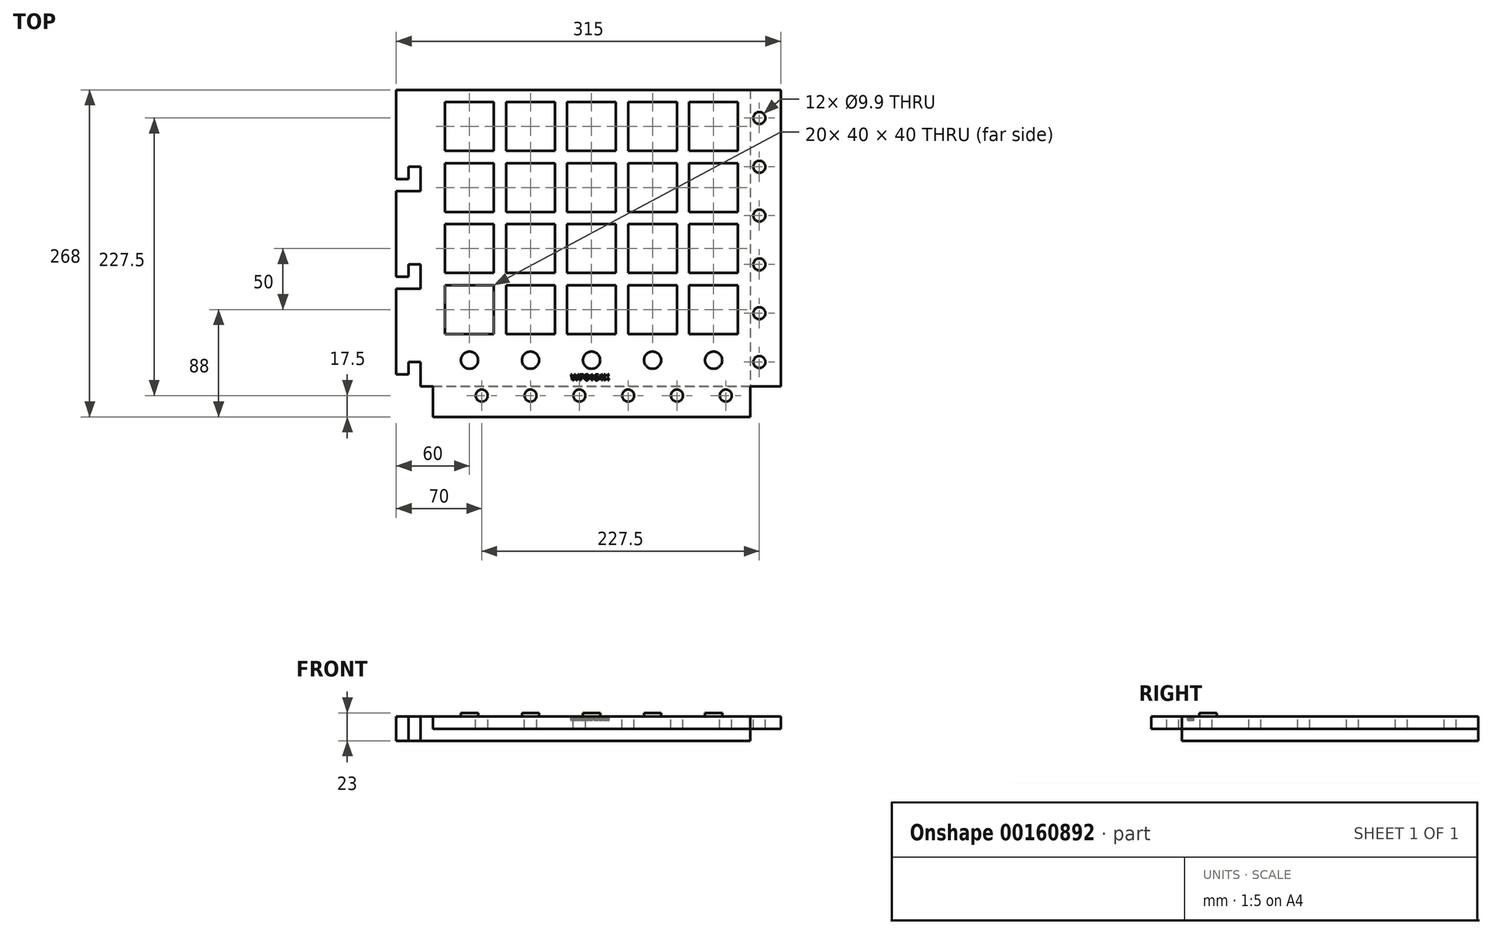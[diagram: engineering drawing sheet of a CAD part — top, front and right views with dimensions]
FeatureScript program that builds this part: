
annotation { "Feature Type Name" : "Feature", "Feature Type Description" : "" }
export const myFeature = defineFeature(function(context is Context, id is Id, definition is map)
    precondition{}
    {
        {
            var Q0;
            Q0=qCreatedBy(makeId("Top.planeOp"),FACE);
            var sketch = newSketch(context, id + "F0", { "sketchPlane" : qUnion([Q0])});
            skLineSegment(sketch, "E0", {"start": v(-205.43, 0) * mm, "end": v(243.02, 0) * mm, "construction": true});
            skLineSegment(sketch, "E1", {"start": v(0, 205.1) * mm, "end": v(0, -211.65) * mm, "construction": true});
            skLineSegment(sketch, "E2.bottom", {"start": v(130, 105) * mm, "end": v(-130, 105) * mm});
            skLineSegment(sketch, "E2.top", {"start": v(130, -105) * mm, "end": v(-130, -105) * mm});
            skLineSegment(sketch, "E2.left", {"start": v(130, 105) * mm, "end": v(130, -105) * mm});
            skLineSegment(sketch, "E2.right", {"start": v(-130, 105) * mm, "end": v(-130, -105) * mm});
            skPoint(sketch, "E2.middle", {"position": v(0, 0) * mm});
            skLineSegment(sketch, "E3.bottom", {"start": v(80, -55) * mm, "end": v(120, -55) * mm});
            skLineSegment(sketch, "E3.top", {"start": v(80, -95) * mm, "end": v(120, -95) * mm});
            skLineSegment(sketch, "E3.left", {"start": v(80, -55) * mm, "end": v(80, -95) * mm});
            skLineSegment(sketch, "E3.right", {"start": v(120, -55) * mm, "end": v(120, -95) * mm});
            skLineSegment(sketch, "E4.0.1.0", {"start": v(80, -5) * mm, "end": v(120, -5) * mm});
            skLineSegment(sketch, "E4.0.1.1", {"start": v(120, -5) * mm, "end": v(120, -45) * mm});
            skLineSegment(sketch, "E4.0.1.2", {"start": v(80, -45) * mm, "end": v(120, -45) * mm});
            skLineSegment(sketch, "E4.0.1.3", {"start": v(80, -5) * mm, "end": v(80, -45) * mm});
            skLineSegment(sketch, "E4.0.2.0", {"start": v(80, 45) * mm, "end": v(120, 45) * mm});
            skLineSegment(sketch, "E4.0.2.1", {"start": v(120, 45) * mm, "end": v(120, 5) * mm});
            skLineSegment(sketch, "E4.0.2.2", {"start": v(80, 5) * mm, "end": v(120, 5) * mm});
            skLineSegment(sketch, "E4.0.2.3", {"start": v(80, 45) * mm, "end": v(80, 5) * mm});
            skLineSegment(sketch, "E4.0.3.0", {"start": v(80, 95) * mm, "end": v(120, 95) * mm});
            skLineSegment(sketch, "E4.0.3.1", {"start": v(120, 95) * mm, "end": v(120, 55) * mm});
            skLineSegment(sketch, "E4.0.3.2", {"start": v(80, 55) * mm, "end": v(120, 55) * mm});
            skLineSegment(sketch, "E4.0.3.3", {"start": v(80, 95) * mm, "end": v(80, 55) * mm});
            skLineSegment(sketch, "E4.1.0.0", {"start": v(30, -55) * mm, "end": v(70, -55) * mm});
            skLineSegment(sketch, "E4.1.0.1", {"start": v(70, -55) * mm, "end": v(70, -95) * mm});
            skLineSegment(sketch, "E4.1.0.2", {"start": v(30, -95) * mm, "end": v(70, -95) * mm});
            skLineSegment(sketch, "E4.1.0.3", {"start": v(30, -55) * mm, "end": v(30, -95) * mm});
            skLineSegment(sketch, "E4.1.1.0", {"start": v(30, -5) * mm, "end": v(70, -5) * mm});
            skLineSegment(sketch, "E4.1.1.1", {"start": v(70, -5) * mm, "end": v(70, -45) * mm});
            skLineSegment(sketch, "E4.1.1.2", {"start": v(30, -45) * mm, "end": v(70, -45) * mm});
            skLineSegment(sketch, "E4.1.1.3", {"start": v(30, -5) * mm, "end": v(30, -45) * mm});
            skLineSegment(sketch, "E4.1.2.0", {"start": v(30, 45) * mm, "end": v(70, 45) * mm});
            skLineSegment(sketch, "E4.1.2.1", {"start": v(70, 45) * mm, "end": v(70, 5) * mm});
            skLineSegment(sketch, "E4.1.2.2", {"start": v(30, 5) * mm, "end": v(70, 5) * mm});
            skLineSegment(sketch, "E4.1.2.3", {"start": v(30, 45) * mm, "end": v(30, 5) * mm});
            skLineSegment(sketch, "E4.1.3.0", {"start": v(30, 95) * mm, "end": v(70, 95) * mm});
            skLineSegment(sketch, "E4.1.3.1", {"start": v(70, 95) * mm, "end": v(70, 55) * mm});
            skLineSegment(sketch, "E4.1.3.2", {"start": v(30, 55) * mm, "end": v(70, 55) * mm});
            skLineSegment(sketch, "E4.1.3.3", {"start": v(30, 95) * mm, "end": v(30, 55) * mm});
            skLineSegment(sketch, "E4.2.0.0", {"start": v(-20, -55) * mm, "end": v(20, -55) * mm});
            skLineSegment(sketch, "E4.2.0.1", {"start": v(20, -55) * mm, "end": v(20, -95) * mm});
            skLineSegment(sketch, "E4.2.0.2", {"start": v(-20, -95) * mm, "end": v(20, -95) * mm});
            skLineSegment(sketch, "E4.2.0.3", {"start": v(-20, -55) * mm, "end": v(-20, -95) * mm});
            skLineSegment(sketch, "E4.2.1.0", {"start": v(-20, -5) * mm, "end": v(20, -5) * mm});
            skLineSegment(sketch, "E4.2.1.1", {"start": v(20, -5) * mm, "end": v(20, -45) * mm});
            skLineSegment(sketch, "E4.2.1.2", {"start": v(-20, -45) * mm, "end": v(20, -45) * mm});
            skLineSegment(sketch, "E4.2.1.3", {"start": v(-20, -5) * mm, "end": v(-20, -45) * mm});
            skLineSegment(sketch, "E4.2.2.0", {"start": v(-20, 45) * mm, "end": v(20, 45) * mm});
            skLineSegment(sketch, "E4.2.2.1", {"start": v(20, 45) * mm, "end": v(20, 5) * mm});
            skLineSegment(sketch, "E4.2.2.2", {"start": v(-20, 5) * mm, "end": v(20, 5) * mm});
            skLineSegment(sketch, "E4.2.2.3", {"start": v(-20, 45) * mm, "end": v(-20, 5) * mm});
            skLineSegment(sketch, "E4.2.3.0", {"start": v(-20, 95) * mm, "end": v(20, 95) * mm});
            skLineSegment(sketch, "E4.2.3.1", {"start": v(20, 95) * mm, "end": v(20, 55) * mm});
            skLineSegment(sketch, "E4.2.3.2", {"start": v(-20, 55) * mm, "end": v(20, 55) * mm});
            skLineSegment(sketch, "E4.2.3.3", {"start": v(-20, 95) * mm, "end": v(-20, 55) * mm});
            skLineSegment(sketch, "E4.3.0.0", {"start": v(-70, -55) * mm, "end": v(-30, -55) * mm});
            skLineSegment(sketch, "E4.3.0.1", {"start": v(-30, -55) * mm, "end": v(-30, -95) * mm});
            skLineSegment(sketch, "E4.3.0.2", {"start": v(-70, -95) * mm, "end": v(-30, -95) * mm});
            skLineSegment(sketch, "E4.3.0.3", {"start": v(-70, -55) * mm, "end": v(-70, -95) * mm});
            skLineSegment(sketch, "E4.3.1.0", {"start": v(-70, -5) * mm, "end": v(-30, -5) * mm});
            skLineSegment(sketch, "E4.3.1.1", {"start": v(-30, -5) * mm, "end": v(-30, -45) * mm});
            skLineSegment(sketch, "E4.3.1.2", {"start": v(-70, -45) * mm, "end": v(-30, -45) * mm});
            skLineSegment(sketch, "E4.3.1.3", {"start": v(-70, -5) * mm, "end": v(-70, -45) * mm});
            skLineSegment(sketch, "E4.3.2.0", {"start": v(-70, 45) * mm, "end": v(-30, 45) * mm});
            skLineSegment(sketch, "E4.3.2.1", {"start": v(-30, 45) * mm, "end": v(-30, 5) * mm});
            skLineSegment(sketch, "E4.3.2.2", {"start": v(-70, 5) * mm, "end": v(-30, 5) * mm});
            skLineSegment(sketch, "E4.3.2.3", {"start": v(-70, 45) * mm, "end": v(-70, 5) * mm});
            skLineSegment(sketch, "E4.3.3.0", {"start": v(-70, 95) * mm, "end": v(-30, 95) * mm});
            skLineSegment(sketch, "E4.3.3.1", {"start": v(-30, 95) * mm, "end": v(-30, 55) * mm});
            skLineSegment(sketch, "E4.3.3.2", {"start": v(-70, 55) * mm, "end": v(-30, 55) * mm});
            skLineSegment(sketch, "E4.3.3.3", {"start": v(-70, 95) * mm, "end": v(-70, 55) * mm});
            skLineSegment(sketch, "E4.4.0.0", {"start": v(-120, -55) * mm, "end": v(-80, -55) * mm});
            skLineSegment(sketch, "E4.4.0.1", {"start": v(-80, -55) * mm, "end": v(-80, -95) * mm});
            skLineSegment(sketch, "E4.4.0.2", {"start": v(-120, -95) * mm, "end": v(-80, -95) * mm});
            skLineSegment(sketch, "E4.4.0.3", {"start": v(-120, -55) * mm, "end": v(-120, -95) * mm});
            skLineSegment(sketch, "E4.4.1.0", {"start": v(-120, -5) * mm, "end": v(-80, -5) * mm});
            skLineSegment(sketch, "E4.4.1.1", {"start": v(-80, -5) * mm, "end": v(-80, -45) * mm});
            skLineSegment(sketch, "E4.4.1.2", {"start": v(-120, -45) * mm, "end": v(-80, -45) * mm});
            skLineSegment(sketch, "E4.4.1.3", {"start": v(-120, -5) * mm, "end": v(-120, -45) * mm});
            skLineSegment(sketch, "E4.4.2.0", {"start": v(-120, 45) * mm, "end": v(-80, 45) * mm});
            skLineSegment(sketch, "E4.4.2.1", {"start": v(-80, 45) * mm, "end": v(-80, 5) * mm});
            skLineSegment(sketch, "E4.4.2.2", {"start": v(-120, 5) * mm, "end": v(-80, 5) * mm});
            skLineSegment(sketch, "E4.4.2.3", {"start": v(-120, 45) * mm, "end": v(-120, 5) * mm});
            skLineSegment(sketch, "E4.4.3.0", {"start": v(-120, 95) * mm, "end": v(-80, 95) * mm});
            skLineSegment(sketch, "E4.4.3.1", {"start": v(-80, 95) * mm, "end": v(-80, 55) * mm});
            skLineSegment(sketch, "E4.4.3.2", {"start": v(-120, 55) * mm, "end": v(-80, 55) * mm});
            skLineSegment(sketch, "E4.4.3.3", {"start": v(-120, 95) * mm, "end": v(-120, 55) * mm});
            skLineSegment(sketch, "E4.direction1", {"start": v(80, -95) * mm, "end": v(30, -95) * mm, "construction": true});
            skLineSegment(sketch, "E4.direction2", {"start": v(80, -95) * mm, "end": v(80, -45) * mm, "construction": true});
            skSolve(sketch);
        }
        {
            var Q0;
            Q0=qSketchRegion(id+"F0",true);
            extrude(context, id + "F1", {"entities" : qUnion([Q0]), "depth" : 20 * mm});
        }
        {
            var Q0;
            Q0=makeQuery(id+"F1.opExtrude","SWEPT_FACE",FACE,{"disambiguationData":[OSD([sQuery(id+"F0.wireOp",EDGE,"E2.top")])]});
            extrude(context, id + "F2", {"entities" : qUnion([Q0]), "operationType" : NewBodyOperationType.ADD, "depth" : 33 * mm});
        }
        {
            var Q0;
            Q0=makeQuery(id+"F2.opExtrude","CAP_FACE",FACE,{"disambiguationData":[OSD([sQuery(id+"F0.wireOp",EDGE,"E2.top")])],"isStart":false});
            var sketch = newSketch(context, id + "F3", { "sketchPlane" : qUnion([Q0])});
            skLineSegment(sketch, "E5.bottom", {"start": v(-130, 20) * mm, "end": v(130, 20) * mm});
            skLineSegment(sketch, "E5.top", {"start": v(-130, 10) * mm, "end": v(130, 10) * mm});
            skLineSegment(sketch, "E5.left", {"start": v(-130, 20) * mm, "end": v(-130, 10) * mm});
            skLineSegment(sketch, "E5.right", {"start": v(130, 20) * mm, "end": v(130, 10) * mm});
            skSolve(sketch);
        }
        {
            var Q0;
            Q0=qSketchRegion(id+"F3",true);
            extrude(context, id + "F4", {"entities" : qUnion([Q0]), "operationType" : NewBodyOperationType.ADD, "depth" : 25 * mm});
        }
        {
            var Q0;
            {var subQ0=sQuery(id+"F0.wireOp",EDGE,"E2.top");Q0=makeQuery(id+"F4.boolean.opBoolean","MERGE",FACE,{"derivedFrom":[makeQuery(id+"F2.boolean.opBoolean","MERGE",FACE,{"derivedFrom":[makeQuery(id+"F1.opExtrude","CAP_FACE",FACE,{"disambiguationData":[OSD([sQuery(id+"F0.wireOp",EDGE,"E2.bottom"),subQ0,sQuery(id+"F0.wireOp",EDGE,"E2.left"),sQuery(id+"F0.wireOp",EDGE,"E2.right"),sQuery(id+"F0.wireOp",EDGE,"E3.bottom"),sQuery(id+"F0.wireOp",EDGE,"E3.top"),sQuery(id+"F0.wireOp",EDGE,"E3.left"),sQuery(id+"F0.wireOp",EDGE,"E3.right"),sQuery(id+"F0.wireOp",EDGE,"E4.0.1.0"),sQuery(id+"F0.wireOp",EDGE,"E4.0.1.1"),sQuery(id+"F0.wireOp",EDGE,"E4.0.1.2"),sQuery(id+"F0.wireOp",EDGE,"E4.0.1.3"),sQuery(id+"F0.wireOp",EDGE,"E4.0.2.0"),sQuery(id+"F0.wireOp",EDGE,"E4.0.2.1"),sQuery(id+"F0.wireOp",EDGE,"E4.0.2.2"),sQuery(id+"F0.wireOp",EDGE,"E4.0.2.3"),sQuery(id+"F0.wireOp",EDGE,"E4.0.3.0"),sQuery(id+"F0.wireOp",EDGE,"E4.0.3.1"),sQuery(id+"F0.wireOp",EDGE,"E4.0.3.2"),sQuery(id+"F0.wireOp",EDGE,"E4.0.3.3"),sQuery(id+"F0.wireOp",EDGE,"E4.1.0.0"),sQuery(id+"F0.wireOp",EDGE,"E4.1.0.1"),sQuery(id+"F0.wireOp",EDGE,"E4.1.0.2"),sQuery(id+"F0.wireOp",EDGE,"E4.1.0.3"),sQuery(id+"F0.wireOp",EDGE,"E4.1.1.0"),sQuery(id+"F0.wireOp",EDGE,"E4.1.1.1"),sQuery(id+"F0.wireOp",EDGE,"E4.1.1.2"),sQuery(id+"F0.wireOp",EDGE,"E4.1.1.3"),sQuery(id+"F0.wireOp",EDGE,"E4.1.2.0"),sQuery(id+"F0.wireOp",EDGE,"E4.1.2.1"),sQuery(id+"F0.wireOp",EDGE,"E4.1.2.2"),sQuery(id+"F0.wireOp",EDGE,"E4.1.2.3"),sQuery(id+"F0.wireOp",EDGE,"E4.1.3.0"),sQuery(id+"F0.wireOp",EDGE,"E4.1.3.1"),sQuery(id+"F0.wireOp",EDGE,"E4.1.3.2"),sQuery(id+"F0.wireOp",EDGE,"E4.1.3.3"),sQuery(id+"F0.wireOp",EDGE,"E4.2.0.0"),sQuery(id+"F0.wireOp",EDGE,"E4.2.0.1"),sQuery(id+"F0.wireOp",EDGE,"E4.2.0.2"),sQuery(id+"F0.wireOp",EDGE,"E4.2.0.3"),sQuery(id+"F0.wireOp",EDGE,"E4.2.1.0"),sQuery(id+"F0.wireOp",EDGE,"E4.2.1.1"),sQuery(id+"F0.wireOp",EDGE,"E4.2.1.2"),sQuery(id+"F0.wireOp",EDGE,"E4.2.1.3"),sQuery(id+"F0.wireOp",EDGE,"E4.2.2.0"),sQuery(id+"F0.wireOp",EDGE,"E4.2.2.1"),sQuery(id+"F0.wireOp",EDGE,"E4.2.2.2"),sQuery(id+"F0.wireOp",EDGE,"E4.2.2.3"),sQuery(id+"F0.wireOp",EDGE,"E4.2.3.0"),sQuery(id+"F0.wireOp",EDGE,"E4.2.3.1"),sQuery(id+"F0.wireOp",EDGE,"E4.2.3.2"),sQuery(id+"F0.wireOp",EDGE,"E4.2.3.3"),sQuery(id+"F0.wireOp",EDGE,"E4.3.0.0"),sQuery(id+"F0.wireOp",EDGE,"E4.3.0.1"),sQuery(id+"F0.wireOp",EDGE,"E4.3.0.2"),sQuery(id+"F0.wireOp",EDGE,"E4.3.0.3"),sQuery(id+"F0.wireOp",EDGE,"E4.3.1.0"),sQuery(id+"F0.wireOp",EDGE,"E4.3.1.1"),sQuery(id+"F0.wireOp",EDGE,"E4.3.1.2"),sQuery(id+"F0.wireOp",EDGE,"E4.3.1.3"),sQuery(id+"F0.wireOp",EDGE,"E4.3.2.0"),sQuery(id+"F0.wireOp",EDGE,"E4.3.2.1"),sQuery(id+"F0.wireOp",EDGE,"E4.3.2.2"),sQuery(id+"F0.wireOp",EDGE,"E4.3.2.3"),sQuery(id+"F0.wireOp",EDGE,"E4.3.3.0"),sQuery(id+"F0.wireOp",EDGE,"E4.3.3.1"),sQuery(id+"F0.wireOp",EDGE,"E4.3.3.2"),sQuery(id+"F0.wireOp",EDGE,"E4.3.3.3"),sQuery(id+"F0.wireOp",EDGE,"E4.4.0.0"),sQuery(id+"F0.wireOp",EDGE,"E4.4.0.1"),sQuery(id+"F0.wireOp",EDGE,"E4.4.0.2"),sQuery(id+"F0.wireOp",EDGE,"E4.4.0.3"),sQuery(id+"F0.wireOp",EDGE,"E4.4.1.0"),sQuery(id+"F0.wireOp",EDGE,"E4.4.1.1"),sQuery(id+"F0.wireOp",EDGE,"E4.4.1.2"),sQuery(id+"F0.wireOp",EDGE,"E4.4.1.3"),sQuery(id+"F0.wireOp",EDGE,"E4.4.2.0"),sQuery(id+"F0.wireOp",EDGE,"E4.4.2.1"),sQuery(id+"F0.wireOp",EDGE,"E4.4.2.2"),sQuery(id+"F0.wireOp",EDGE,"E4.4.2.3"),sQuery(id+"F0.wireOp",EDGE,"E4.4.3.0"),sQuery(id+"F0.wireOp",EDGE,"E4.4.3.1"),sQuery(id+"F0.wireOp",EDGE,"E4.4.3.2"),sQuery(id+"F0.wireOp",EDGE,"E4.4.3.3")])],"isStart":false}),makeQuery(id+"F2.opExtrude","SWEPT_FACE",FACE,{"disambiguationData":[OSD([subQ0]),TDD([makeQuery(id+"F1.opExtrude","CAP_EDGE",EDGE,{"disambiguationData":[OSD([subQ0])],"isStart":false})])]})]}),makeQuery(id+"F4.opExtrude","SWEPT_FACE",FACE,{"disambiguationData":[OSD([sQuery(id+"F3.wireOp",EDGE,"E5.bottom")])]})]});}
            var sketch = newSketch(context, id + "F5", { "sketchPlane" : qUnion([Q0])});
            skCircle(sketch, "E6", {"center": v(110, -145.5) * mm, "radius": 4.95 * mm});
            skLineSegment(sketch, "E7", {"start": v(-121.54, -145.5) * mm, "end": v(178.6, -145.5) * mm, "construction": true});
            skLineSegment(sketch, "E8", {"start": v(110, -159.43) * mm, "end": v(110, -131.93) * mm, "construction": true});
            skCircle(sketch, "E9.1.0.0", {"center": v(70, -145.5) * mm, "radius": 4.95 * mm});
            skCircle(sketch, "E9.2.0.0", {"center": v(30, -145.5) * mm, "radius": 4.95 * mm});
            skCircle(sketch, "E9.3.0.0", {"center": v(-10, -145.5) * mm, "radius": 4.95 * mm});
            skCircle(sketch, "E9.4.0.0", {"center": v(-50, -145.5) * mm, "radius": 4.95 * mm});
            skCircle(sketch, "E9.5.0.0", {"center": v(-90, -145.5) * mm, "radius": 4.95 * mm});
            skLineSegment(sketch, "E9.direction1", {"start": v(110, -145.5) * mm, "end": v(70, -145.5) * mm, "construction": true});
            skSolve(sketch);
        }
        {
            var Q0;
            Q0=qSketchRegion(id+"F5",true);
            extrude(context, id + "F6", {"entities" : qUnion([Q0]), "operationType" : NewBodyOperationType.REMOVE, "oppositeDirection" : true, "depth" : 25 * mm});
        }
        {
            var Q0;
            {var subQ0=sQuery(id+"F0.wireOp",EDGE,"E2.left");Q0=makeQuery(id+"F4.boolean.opBoolean","MERGE",FACE,{"derivedFrom":[makeQuery(id+"F2.boolean.opBoolean","MERGE",FACE,{"derivedFrom":[makeQuery(id+"F1.opExtrude","SWEPT_FACE",FACE,{"disambiguationData":[OSD([subQ0])]}),makeQuery(id+"F2.opExtrude","SWEPT_FACE",FACE,{"disambiguationData":[OSD([sQuery(id+"F0.wireOp",EDGE,"E2.top"),subQ0])]})]}),makeQuery(id+"F4.opExtrude","SWEPT_FACE",FACE,{"disambiguationData":[OSD([sQuery(id+"F3.wireOp",EDGE,"E5.right")])]})]});}
            var sketch = newSketch(context, id + "F7", { "sketchPlane" : qUnion([Q0])});
            skLineSegment(sketch, "E10.bottom", {"start": v(105, 20) * mm, "end": v(-138, 20) * mm});
            skLineSegment(sketch, "E10.top", {"start": v(105, 10) * mm, "end": v(-138, 10) * mm});
            skLineSegment(sketch, "E10.left", {"start": v(105, 20) * mm, "end": v(105, 10) * mm});
            skLineSegment(sketch, "E10.right", {"start": v(-138, 20) * mm, "end": v(-138, 10) * mm});
            skSolve(sketch);
        }
        {
            var Q0;
            Q0=qSketchRegion(id+"F7",true);
            extrude(context, id + "F8", {"entities" : qUnion([Q0]), "operationType" : NewBodyOperationType.ADD, "depth" : 25 * mm});
        }
        {
            var Q0;
            {var subQ0=sQuery(id+"F0.wireOp",EDGE,"E2.top");Q0=makeQuery(id+"F8.boolean.opBoolean","MERGE",FACE,{"derivedFrom":[makeQuery(id+"F4.boolean.opBoolean","MERGE",FACE,{"derivedFrom":[makeQuery(id+"F2.boolean.opBoolean","MERGE",FACE,{"derivedFrom":[makeQuery(id+"F1.opExtrude","CAP_FACE",FACE,{"disambiguationData":[OSD([sQuery(id+"F0.wireOp",EDGE,"E2.bottom"),subQ0,sQuery(id+"F0.wireOp",EDGE,"E2.left"),sQuery(id+"F0.wireOp",EDGE,"E2.right"),sQuery(id+"F0.wireOp",EDGE,"E3.bottom"),sQuery(id+"F0.wireOp",EDGE,"E3.top"),sQuery(id+"F0.wireOp",EDGE,"E3.left"),sQuery(id+"F0.wireOp",EDGE,"E3.right"),sQuery(id+"F0.wireOp",EDGE,"E4.0.1.0"),sQuery(id+"F0.wireOp",EDGE,"E4.0.1.1"),sQuery(id+"F0.wireOp",EDGE,"E4.0.1.2"),sQuery(id+"F0.wireOp",EDGE,"E4.0.1.3"),sQuery(id+"F0.wireOp",EDGE,"E4.0.2.0"),sQuery(id+"F0.wireOp",EDGE,"E4.0.2.1"),sQuery(id+"F0.wireOp",EDGE,"E4.0.2.2"),sQuery(id+"F0.wireOp",EDGE,"E4.0.2.3"),sQuery(id+"F0.wireOp",EDGE,"E4.0.3.0"),sQuery(id+"F0.wireOp",EDGE,"E4.0.3.1"),sQuery(id+"F0.wireOp",EDGE,"E4.0.3.2"),sQuery(id+"F0.wireOp",EDGE,"E4.0.3.3"),sQuery(id+"F0.wireOp",EDGE,"E4.1.0.0"),sQuery(id+"F0.wireOp",EDGE,"E4.1.0.1"),sQuery(id+"F0.wireOp",EDGE,"E4.1.0.2"),sQuery(id+"F0.wireOp",EDGE,"E4.1.0.3"),sQuery(id+"F0.wireOp",EDGE,"E4.1.1.0"),sQuery(id+"F0.wireOp",EDGE,"E4.1.1.1"),sQuery(id+"F0.wireOp",EDGE,"E4.1.1.2"),sQuery(id+"F0.wireOp",EDGE,"E4.1.1.3"),sQuery(id+"F0.wireOp",EDGE,"E4.1.2.0"),sQuery(id+"F0.wireOp",EDGE,"E4.1.2.1"),sQuery(id+"F0.wireOp",EDGE,"E4.1.2.2"),sQuery(id+"F0.wireOp",EDGE,"E4.1.2.3"),sQuery(id+"F0.wireOp",EDGE,"E4.1.3.0"),sQuery(id+"F0.wireOp",EDGE,"E4.1.3.1"),sQuery(id+"F0.wireOp",EDGE,"E4.1.3.2"),sQuery(id+"F0.wireOp",EDGE,"E4.1.3.3"),sQuery(id+"F0.wireOp",EDGE,"E4.2.0.0"),sQuery(id+"F0.wireOp",EDGE,"E4.2.0.1"),sQuery(id+"F0.wireOp",EDGE,"E4.2.0.2"),sQuery(id+"F0.wireOp",EDGE,"E4.2.0.3"),sQuery(id+"F0.wireOp",EDGE,"E4.2.1.0"),sQuery(id+"F0.wireOp",EDGE,"E4.2.1.1"),sQuery(id+"F0.wireOp",EDGE,"E4.2.1.2"),sQuery(id+"F0.wireOp",EDGE,"E4.2.1.3"),sQuery(id+"F0.wireOp",EDGE,"E4.2.2.0"),sQuery(id+"F0.wireOp",EDGE,"E4.2.2.1"),sQuery(id+"F0.wireOp",EDGE,"E4.2.2.2"),sQuery(id+"F0.wireOp",EDGE,"E4.2.2.3"),sQuery(id+"F0.wireOp",EDGE,"E4.2.3.0"),sQuery(id+"F0.wireOp",EDGE,"E4.2.3.1"),sQuery(id+"F0.wireOp",EDGE,"E4.2.3.2"),sQuery(id+"F0.wireOp",EDGE,"E4.2.3.3"),sQuery(id+"F0.wireOp",EDGE,"E4.3.0.0"),sQuery(id+"F0.wireOp",EDGE,"E4.3.0.1"),sQuery(id+"F0.wireOp",EDGE,"E4.3.0.2"),sQuery(id+"F0.wireOp",EDGE,"E4.3.0.3"),sQuery(id+"F0.wireOp",EDGE,"E4.3.1.0"),sQuery(id+"F0.wireOp",EDGE,"E4.3.1.1"),sQuery(id+"F0.wireOp",EDGE,"E4.3.1.2"),sQuery(id+"F0.wireOp",EDGE,"E4.3.1.3"),sQuery(id+"F0.wireOp",EDGE,"E4.3.2.0"),sQuery(id+"F0.wireOp",EDGE,"E4.3.2.1"),sQuery(id+"F0.wireOp",EDGE,"E4.3.2.2"),sQuery(id+"F0.wireOp",EDGE,"E4.3.2.3"),sQuery(id+"F0.wireOp",EDGE,"E4.3.3.0"),sQuery(id+"F0.wireOp",EDGE,"E4.3.3.1"),sQuery(id+"F0.wireOp",EDGE,"E4.3.3.2"),sQuery(id+"F0.wireOp",EDGE,"E4.3.3.3"),sQuery(id+"F0.wireOp",EDGE,"E4.4.0.0"),sQuery(id+"F0.wireOp",EDGE,"E4.4.0.1"),sQuery(id+"F0.wireOp",EDGE,"E4.4.0.2"),sQuery(id+"F0.wireOp",EDGE,"E4.4.0.3"),sQuery(id+"F0.wireOp",EDGE,"E4.4.1.0"),sQuery(id+"F0.wireOp",EDGE,"E4.4.1.1"),sQuery(id+"F0.wireOp",EDGE,"E4.4.1.2"),sQuery(id+"F0.wireOp",EDGE,"E4.4.1.3"),sQuery(id+"F0.wireOp",EDGE,"E4.4.2.0"),sQuery(id+"F0.wireOp",EDGE,"E4.4.2.1"),sQuery(id+"F0.wireOp",EDGE,"E4.4.2.2"),sQuery(id+"F0.wireOp",EDGE,"E4.4.2.3"),sQuery(id+"F0.wireOp",EDGE,"E4.4.3.0"),sQuery(id+"F0.wireOp",EDGE,"E4.4.3.1"),sQuery(id+"F0.wireOp",EDGE,"E4.4.3.2"),sQuery(id+"F0.wireOp",EDGE,"E4.4.3.3")])],"isStart":false}),makeQuery(id+"F2.opExtrude","SWEPT_FACE",FACE,{"disambiguationData":[OSD([subQ0]),TDD([makeQuery(id+"F1.opExtrude","CAP_EDGE",EDGE,{"disambiguationData":[OSD([subQ0])],"isStart":false})])]})]}),makeQuery(id+"F4.opExtrude","SWEPT_FACE",FACE,{"disambiguationData":[OSD([sQuery(id+"F3.wireOp",EDGE,"E5.bottom")])]})]}),makeQuery(id+"F8.opExtrude","SWEPT_FACE",FACE,{"disambiguationData":[OSD([sQuery(id+"F7.wireOp",EDGE,"E10.bottom")])]})]});}
            var sketch = newSketch(context, id + "F9", { "sketchPlane" : qUnion([Q0])});
            skLineSegment(sketch, "E11", {"start": v(137.5, -148.15) * mm, "end": v(137.5, 118.27) * mm, "construction": true});
            skCircle(sketch, "E12", {"center": v(137.5, -118) * mm, "radius": 4.95 * mm});
            skLineSegment(sketch, "E13", {"start": v(128.57, -118) * mm, "end": v(148.12, -118) * mm, "construction": true});
            skCircle(sketch, "E14.0.1.0", {"center": v(137.5, -78) * mm, "radius": 4.95 * mm});
            skCircle(sketch, "E14.0.2.0", {"center": v(137.5, -38) * mm, "radius": 4.95 * mm});
            skCircle(sketch, "E14.0.3.0", {"center": v(137.5, 2) * mm, "radius": 4.95 * mm});
            skCircle(sketch, "E14.0.4.0", {"center": v(137.5, 42) * mm, "radius": 4.95 * mm});
            skCircle(sketch, "E14.0.5.0", {"center": v(137.5, 82) * mm, "radius": 4.95 * mm});
            skLineSegment(sketch, "E14.direction1", {"start": v(137.5, -118) * mm, "end": v(150.25, -118) * mm, "construction": true});
            skLineSegment(sketch, "E14.direction2", {"start": v(137.5, -118) * mm, "end": v(137.5, -78) * mm, "construction": true});
            skSolve(sketch);
        }
        {
            var Q0;
            Q0=qSketchRegion(id+"F9",true);
            extrude(context, id + "F10", {"entities" : qUnion([Q0]), "operationType" : NewBodyOperationType.REMOVE, "oppositeDirection" : true, "depth" : 25 * mm});
        }
        {
            var Q0;
            {var subQ0=sQuery(id+"F0.wireOp",EDGE,"E2.right");Q0=makeQuery(id+"F4.boolean.opBoolean","MERGE",FACE,{"derivedFrom":[makeQuery(id+"F2.boolean.opBoolean","MERGE",FACE,{"derivedFrom":[makeQuery(id+"F1.opExtrude","SWEPT_FACE",FACE,{"disambiguationData":[OSD([subQ0])]}),makeQuery(id+"F2.opExtrude","SWEPT_FACE",FACE,{"disambiguationData":[OSD([sQuery(id+"F0.wireOp",EDGE,"E2.top"),subQ0])]})]}),makeQuery(id+"F4.opExtrude","SWEPT_FACE",FACE,{"disambiguationData":[OSD([sQuery(id+"F3.wireOp",EDGE,"E5.left")])]})]});}
            var sketch = newSketch(context, id + "F11", { "sketchPlane" : qUnion([Q0])});
            skLineSegment(sketch, "E15.bottom", {"start": v(-105, 20) * mm, "end": v(138, 20) * mm});
            skLineSegment(sketch, "E15.top", {"start": v(-105, 0) * mm, "end": v(138, 0) * mm});
            skLineSegment(sketch, "E15.left", {"start": v(-105, 20) * mm, "end": v(-105, 0) * mm});
            skLineSegment(sketch, "E15.right", {"start": v(138, 20) * mm, "end": v(138, 0) * mm});
            skSolve(sketch);
        }
        {
            var Q0;
            Q0=qSketchRegion(id+"F11",true);
            extrude(context, id + "F12", {"entities" : qUnion([Q0]), "operationType" : NewBodyOperationType.ADD, "depth" : 30 * mm});
        }
        {
            var Q0;
            {var subQ0=sQuery(id+"F0.wireOp",EDGE,"E2.top");Q0=makeQuery(id+"F12.boolean.opBoolean","MERGE",FACE,{"derivedFrom":[makeQuery(id+"F8.boolean.opBoolean","MERGE",FACE,{"derivedFrom":[makeQuery(id+"F4.boolean.opBoolean","MERGE",FACE,{"derivedFrom":[makeQuery(id+"F2.boolean.opBoolean","MERGE",FACE,{"derivedFrom":[makeQuery(id+"F1.opExtrude","CAP_FACE",FACE,{"disambiguationData":[OSD([sQuery(id+"F0.wireOp",EDGE,"E2.bottom"),subQ0,sQuery(id+"F0.wireOp",EDGE,"E2.left"),sQuery(id+"F0.wireOp",EDGE,"E2.right"),sQuery(id+"F0.wireOp",EDGE,"E3.bottom"),sQuery(id+"F0.wireOp",EDGE,"E3.top"),sQuery(id+"F0.wireOp",EDGE,"E3.left"),sQuery(id+"F0.wireOp",EDGE,"E3.right"),sQuery(id+"F0.wireOp",EDGE,"E4.0.1.0"),sQuery(id+"F0.wireOp",EDGE,"E4.0.1.1"),sQuery(id+"F0.wireOp",EDGE,"E4.0.1.2"),sQuery(id+"F0.wireOp",EDGE,"E4.0.1.3"),sQuery(id+"F0.wireOp",EDGE,"E4.0.2.0"),sQuery(id+"F0.wireOp",EDGE,"E4.0.2.1"),sQuery(id+"F0.wireOp",EDGE,"E4.0.2.2"),sQuery(id+"F0.wireOp",EDGE,"E4.0.2.3"),sQuery(id+"F0.wireOp",EDGE,"E4.0.3.0"),sQuery(id+"F0.wireOp",EDGE,"E4.0.3.1"),sQuery(id+"F0.wireOp",EDGE,"E4.0.3.2"),sQuery(id+"F0.wireOp",EDGE,"E4.0.3.3"),sQuery(id+"F0.wireOp",EDGE,"E4.1.0.0"),sQuery(id+"F0.wireOp",EDGE,"E4.1.0.1"),sQuery(id+"F0.wireOp",EDGE,"E4.1.0.2"),sQuery(id+"F0.wireOp",EDGE,"E4.1.0.3"),sQuery(id+"F0.wireOp",EDGE,"E4.1.1.0"),sQuery(id+"F0.wireOp",EDGE,"E4.1.1.1"),sQuery(id+"F0.wireOp",EDGE,"E4.1.1.2"),sQuery(id+"F0.wireOp",EDGE,"E4.1.1.3"),sQuery(id+"F0.wireOp",EDGE,"E4.1.2.0"),sQuery(id+"F0.wireOp",EDGE,"E4.1.2.1"),sQuery(id+"F0.wireOp",EDGE,"E4.1.2.2"),sQuery(id+"F0.wireOp",EDGE,"E4.1.2.3"),sQuery(id+"F0.wireOp",EDGE,"E4.1.3.0"),sQuery(id+"F0.wireOp",EDGE,"E4.1.3.1"),sQuery(id+"F0.wireOp",EDGE,"E4.1.3.2"),sQuery(id+"F0.wireOp",EDGE,"E4.1.3.3"),sQuery(id+"F0.wireOp",EDGE,"E4.2.0.0"),sQuery(id+"F0.wireOp",EDGE,"E4.2.0.1"),sQuery(id+"F0.wireOp",EDGE,"E4.2.0.2"),sQuery(id+"F0.wireOp",EDGE,"E4.2.0.3"),sQuery(id+"F0.wireOp",EDGE,"E4.2.1.0"),sQuery(id+"F0.wireOp",EDGE,"E4.2.1.1"),sQuery(id+"F0.wireOp",EDGE,"E4.2.1.2"),sQuery(id+"F0.wireOp",EDGE,"E4.2.1.3"),sQuery(id+"F0.wireOp",EDGE,"E4.2.2.0"),sQuery(id+"F0.wireOp",EDGE,"E4.2.2.1"),sQuery(id+"F0.wireOp",EDGE,"E4.2.2.2"),sQuery(id+"F0.wireOp",EDGE,"E4.2.2.3"),sQuery(id+"F0.wireOp",EDGE,"E4.2.3.0"),sQuery(id+"F0.wireOp",EDGE,"E4.2.3.1"),sQuery(id+"F0.wireOp",EDGE,"E4.2.3.2"),sQuery(id+"F0.wireOp",EDGE,"E4.2.3.3"),sQuery(id+"F0.wireOp",EDGE,"E4.3.0.0"),sQuery(id+"F0.wireOp",EDGE,"E4.3.0.1"),sQuery(id+"F0.wireOp",EDGE,"E4.3.0.2"),sQuery(id+"F0.wireOp",EDGE,"E4.3.0.3"),sQuery(id+"F0.wireOp",EDGE,"E4.3.1.0"),sQuery(id+"F0.wireOp",EDGE,"E4.3.1.1"),sQuery(id+"F0.wireOp",EDGE,"E4.3.1.2"),sQuery(id+"F0.wireOp",EDGE,"E4.3.1.3"),sQuery(id+"F0.wireOp",EDGE,"E4.3.2.0"),sQuery(id+"F0.wireOp",EDGE,"E4.3.2.1"),sQuery(id+"F0.wireOp",EDGE,"E4.3.2.2"),sQuery(id+"F0.wireOp",EDGE,"E4.3.2.3"),sQuery(id+"F0.wireOp",EDGE,"E4.3.3.0"),sQuery(id+"F0.wireOp",EDGE,"E4.3.3.1"),sQuery(id+"F0.wireOp",EDGE,"E4.3.3.2"),sQuery(id+"F0.wireOp",EDGE,"E4.3.3.3"),sQuery(id+"F0.wireOp",EDGE,"E4.4.0.0"),sQuery(id+"F0.wireOp",EDGE,"E4.4.0.1"),sQuery(id+"F0.wireOp",EDGE,"E4.4.0.2"),sQuery(id+"F0.wireOp",EDGE,"E4.4.0.3"),sQuery(id+"F0.wireOp",EDGE,"E4.4.1.0"),sQuery(id+"F0.wireOp",EDGE,"E4.4.1.1"),sQuery(id+"F0.wireOp",EDGE,"E4.4.1.2"),sQuery(id+"F0.wireOp",EDGE,"E4.4.1.3"),sQuery(id+"F0.wireOp",EDGE,"E4.4.2.0"),sQuery(id+"F0.wireOp",EDGE,"E4.4.2.1"),sQuery(id+"F0.wireOp",EDGE,"E4.4.2.2"),sQuery(id+"F0.wireOp",EDGE,"E4.4.2.3"),sQuery(id+"F0.wireOp",EDGE,"E4.4.3.0"),sQuery(id+"F0.wireOp",EDGE,"E4.4.3.1"),sQuery(id+"F0.wireOp",EDGE,"E4.4.3.2"),sQuery(id+"F0.wireOp",EDGE,"E4.4.3.3")])],"isStart":false}),makeQuery(id+"F2.opExtrude","SWEPT_FACE",FACE,{"disambiguationData":[OSD([subQ0]),TDD([makeQuery(id+"F1.opExtrude","CAP_EDGE",EDGE,{"disambiguationData":[OSD([subQ0])],"isStart":false})])]})]}),makeQuery(id+"F4.opExtrude","SWEPT_FACE",FACE,{"disambiguationData":[OSD([sQuery(id+"F3.wireOp",EDGE,"E5.bottom")])]})]}),makeQuery(id+"F8.opExtrude","SWEPT_FACE",FACE,{"disambiguationData":[OSD([sQuery(id+"F7.wireOp",EDGE,"E10.bottom")])]})]}),makeQuery(id+"F12.opExtrude","SWEPT_FACE",FACE,{"disambiguationData":[OSD([sQuery(id+"F11.wireOp",EDGE,"E15.bottom")])]})]});}
            var sketch = newSketch(context, id + "F13", { "sketchPlane" : qUnion([Q0])});
            skLineSegment(sketch, "E16", {"start": v(-160, -138) * mm, "end": v(-160, -128) * mm});
            skLineSegment(sketch, "E17", {"start": v(-160, -128) * mm, "end": v(-150, -128) * mm});
            skLineSegment(sketch, "E18", {"start": v(-150, -128) * mm, "end": v(-150, -118) * mm});
            skLineSegment(sketch, "E19", {"start": v(-150, -118) * mm, "end": v(-140, -118) * mm});
            skLineSegment(sketch, "E20", {"start": v(-140, -118) * mm, "end": v(-140, -138) * mm});
            skLineSegment(sketch, "E21", {"start": v(-140, -138) * mm, "end": v(-160, -138) * mm});
            skLineSegment(sketch, "E22.0.1.0", {"start": v(-140, -38) * mm, "end": v(-140, -58) * mm});
            skLineSegment(sketch, "E22.0.1.1", {"start": v(-140, -58) * mm, "end": v(-160, -58) * mm});
            skLineSegment(sketch, "E22.0.1.2", {"start": v(-150, -38) * mm, "end": v(-140, -38) * mm});
            skLineSegment(sketch, "E22.0.1.3", {"start": v(-150, -48) * mm, "end": v(-150, -38) * mm});
            skLineSegment(sketch, "E22.0.1.4", {"start": v(-160, -48) * mm, "end": v(-150, -48) * mm});
            skLineSegment(sketch, "E22.0.1.5", {"start": v(-160, -58) * mm, "end": v(-160, -48) * mm});
            skLineSegment(sketch, "E22.0.2.0", {"start": v(-140, 42) * mm, "end": v(-140, 22) * mm});
            skLineSegment(sketch, "E22.0.2.1", {"start": v(-140, 22) * mm, "end": v(-160, 22) * mm});
            skLineSegment(sketch, "E22.0.2.2", {"start": v(-150, 42) * mm, "end": v(-140, 42) * mm});
            skLineSegment(sketch, "E22.0.2.3", {"start": v(-150, 32) * mm, "end": v(-150, 42) * mm});
            skLineSegment(sketch, "E22.0.2.4", {"start": v(-160, 32) * mm, "end": v(-150, 32) * mm});
            skLineSegment(sketch, "E22.0.2.5", {"start": v(-160, 22) * mm, "end": v(-160, 32) * mm});
            skLineSegment(sketch, "E22.direction1", {"start": v(-160, -138) * mm, "end": v(-135, -138) * mm, "construction": true});
            skLineSegment(sketch, "E22.direction2", {"start": v(-160, -138) * mm, "end": v(-160, -58) * mm, "construction": true});
            skSolve(sketch);
        }
        {
            var Q0;
            Q0=qSketchRegion(id+"F13",true);
            extrude(context, id + "F14", {"entities" : qUnion([Q0]), "operationType" : NewBodyOperationType.REMOVE, "oppositeDirection" : true, "depth" : 25 * mm});
        }
        {
            var Q0;
            {var subQ0=sQuery(id+"F0.wireOp",EDGE,"E2.top");Q0=makeQuery(id+"F12.boolean.opBoolean","MERGE",FACE,{"derivedFrom":[makeQuery(id+"F8.boolean.opBoolean","MERGE",FACE,{"derivedFrom":[makeQuery(id+"F4.boolean.opBoolean","MERGE",FACE,{"derivedFrom":[makeQuery(id+"F2.boolean.opBoolean","MERGE",FACE,{"derivedFrom":[makeQuery(id+"F1.opExtrude","CAP_FACE",FACE,{"disambiguationData":[OSD([sQuery(id+"F0.wireOp",EDGE,"E2.bottom"),subQ0,sQuery(id+"F0.wireOp",EDGE,"E2.left"),sQuery(id+"F0.wireOp",EDGE,"E2.right"),sQuery(id+"F0.wireOp",EDGE,"E3.bottom"),sQuery(id+"F0.wireOp",EDGE,"E3.top"),sQuery(id+"F0.wireOp",EDGE,"E3.left"),sQuery(id+"F0.wireOp",EDGE,"E3.right"),sQuery(id+"F0.wireOp",EDGE,"E4.0.1.0"),sQuery(id+"F0.wireOp",EDGE,"E4.0.1.1"),sQuery(id+"F0.wireOp",EDGE,"E4.0.1.2"),sQuery(id+"F0.wireOp",EDGE,"E4.0.1.3"),sQuery(id+"F0.wireOp",EDGE,"E4.0.2.0"),sQuery(id+"F0.wireOp",EDGE,"E4.0.2.1"),sQuery(id+"F0.wireOp",EDGE,"E4.0.2.2"),sQuery(id+"F0.wireOp",EDGE,"E4.0.2.3"),sQuery(id+"F0.wireOp",EDGE,"E4.0.3.0"),sQuery(id+"F0.wireOp",EDGE,"E4.0.3.1"),sQuery(id+"F0.wireOp",EDGE,"E4.0.3.2"),sQuery(id+"F0.wireOp",EDGE,"E4.0.3.3"),sQuery(id+"F0.wireOp",EDGE,"E4.1.0.0"),sQuery(id+"F0.wireOp",EDGE,"E4.1.0.1"),sQuery(id+"F0.wireOp",EDGE,"E4.1.0.2"),sQuery(id+"F0.wireOp",EDGE,"E4.1.0.3"),sQuery(id+"F0.wireOp",EDGE,"E4.1.1.0"),sQuery(id+"F0.wireOp",EDGE,"E4.1.1.1"),sQuery(id+"F0.wireOp",EDGE,"E4.1.1.2"),sQuery(id+"F0.wireOp",EDGE,"E4.1.1.3"),sQuery(id+"F0.wireOp",EDGE,"E4.1.2.0"),sQuery(id+"F0.wireOp",EDGE,"E4.1.2.1"),sQuery(id+"F0.wireOp",EDGE,"E4.1.2.2"),sQuery(id+"F0.wireOp",EDGE,"E4.1.2.3"),sQuery(id+"F0.wireOp",EDGE,"E4.1.3.0"),sQuery(id+"F0.wireOp",EDGE,"E4.1.3.1"),sQuery(id+"F0.wireOp",EDGE,"E4.1.3.2"),sQuery(id+"F0.wireOp",EDGE,"E4.1.3.3"),sQuery(id+"F0.wireOp",EDGE,"E4.2.0.0"),sQuery(id+"F0.wireOp",EDGE,"E4.2.0.1"),sQuery(id+"F0.wireOp",EDGE,"E4.2.0.2"),sQuery(id+"F0.wireOp",EDGE,"E4.2.0.3"),sQuery(id+"F0.wireOp",EDGE,"E4.2.1.0"),sQuery(id+"F0.wireOp",EDGE,"E4.2.1.1"),sQuery(id+"F0.wireOp",EDGE,"E4.2.1.2"),sQuery(id+"F0.wireOp",EDGE,"E4.2.1.3"),sQuery(id+"F0.wireOp",EDGE,"E4.2.2.0"),sQuery(id+"F0.wireOp",EDGE,"E4.2.2.1"),sQuery(id+"F0.wireOp",EDGE,"E4.2.2.2"),sQuery(id+"F0.wireOp",EDGE,"E4.2.2.3"),sQuery(id+"F0.wireOp",EDGE,"E4.2.3.0"),sQuery(id+"F0.wireOp",EDGE,"E4.2.3.1"),sQuery(id+"F0.wireOp",EDGE,"E4.2.3.2"),sQuery(id+"F0.wireOp",EDGE,"E4.2.3.3"),sQuery(id+"F0.wireOp",EDGE,"E4.3.0.0"),sQuery(id+"F0.wireOp",EDGE,"E4.3.0.1"),sQuery(id+"F0.wireOp",EDGE,"E4.3.0.2"),sQuery(id+"F0.wireOp",EDGE,"E4.3.0.3"),sQuery(id+"F0.wireOp",EDGE,"E4.3.1.0"),sQuery(id+"F0.wireOp",EDGE,"E4.3.1.1"),sQuery(id+"F0.wireOp",EDGE,"E4.3.1.2"),sQuery(id+"F0.wireOp",EDGE,"E4.3.1.3"),sQuery(id+"F0.wireOp",EDGE,"E4.3.2.0"),sQuery(id+"F0.wireOp",EDGE,"E4.3.2.1"),sQuery(id+"F0.wireOp",EDGE,"E4.3.2.2"),sQuery(id+"F0.wireOp",EDGE,"E4.3.2.3"),sQuery(id+"F0.wireOp",EDGE,"E4.3.3.0"),sQuery(id+"F0.wireOp",EDGE,"E4.3.3.1"),sQuery(id+"F0.wireOp",EDGE,"E4.3.3.2"),sQuery(id+"F0.wireOp",EDGE,"E4.3.3.3"),sQuery(id+"F0.wireOp",EDGE,"E4.4.0.0"),sQuery(id+"F0.wireOp",EDGE,"E4.4.0.1"),sQuery(id+"F0.wireOp",EDGE,"E4.4.0.2"),sQuery(id+"F0.wireOp",EDGE,"E4.4.0.3"),sQuery(id+"F0.wireOp",EDGE,"E4.4.1.0"),sQuery(id+"F0.wireOp",EDGE,"E4.4.1.1"),sQuery(id+"F0.wireOp",EDGE,"E4.4.1.2"),sQuery(id+"F0.wireOp",EDGE,"E4.4.1.3"),sQuery(id+"F0.wireOp",EDGE,"E4.4.2.0"),sQuery(id+"F0.wireOp",EDGE,"E4.4.2.1"),sQuery(id+"F0.wireOp",EDGE,"E4.4.2.2"),sQuery(id+"F0.wireOp",EDGE,"E4.4.2.3"),sQuery(id+"F0.wireOp",EDGE,"E4.4.3.0"),sQuery(id+"F0.wireOp",EDGE,"E4.4.3.1"),sQuery(id+"F0.wireOp",EDGE,"E4.4.3.2"),sQuery(id+"F0.wireOp",EDGE,"E4.4.3.3")])],"isStart":false}),makeQuery(id+"F2.opExtrude","SWEPT_FACE",FACE,{"disambiguationData":[OSD([subQ0]),TDD([makeQuery(id+"F1.opExtrude","CAP_EDGE",EDGE,{"disambiguationData":[OSD([subQ0])],"isStart":false})])]})]}),makeQuery(id+"F4.opExtrude","SWEPT_FACE",FACE,{"disambiguationData":[OSD([sQuery(id+"F3.wireOp",EDGE,"E5.bottom")])]})]}),makeQuery(id+"F8.opExtrude","SWEPT_FACE",FACE,{"disambiguationData":[OSD([sQuery(id+"F7.wireOp",EDGE,"E10.bottom")])]})]}),makeQuery(id+"F12.opExtrude","SWEPT_FACE",FACE,{"disambiguationData":[OSD([sQuery(id+"F11.wireOp",EDGE,"E15.bottom")])]})]});}
            var sketch = newSketch(context, id + "F15", { "sketchPlane" : qUnion([Q0])});
            skLineSegment(sketch, "E23", {"start": v(-176.3, -116.5) * mm, "end": v(160.59, -116.5) * mm, "construction": true});
            skCircle(sketch, "E24", {"center": v(100, -116.5) * mm, "radius": 7.05 * mm});
            skCircle(sketch, "E25.1.0.0", {"center": v(50, -116.5) * mm, "radius": 7.05 * mm});
            skCircle(sketch, "E25.2.0.0", {"center": v(0, -116.5) * mm, "radius": 7.05 * mm});
            skCircle(sketch, "E25.3.0.0", {"center": v(-50, -116.5) * mm, "radius": 7.05 * mm});
            skCircle(sketch, "E25.4.0.0", {"center": v(-100, -116.5) * mm, "radius": 7.05 * mm});
            skLineSegment(sketch, "E25.direction1", {"start": v(100, -116.5) * mm, "end": v(50, -116.5) * mm, "construction": true});
            skSolve(sketch);
        }
        {
            var Q0;
            Q0=qSketchRegion(id+"F15",true);
            extrude(context, id + "F16", {"entities" : qUnion([Q0]), "operationType" : NewBodyOperationType.ADD, "depth" : 3 * mm});
        }
        {
            var Q0;
            {var subQ0=sQuery(id+"F0.wireOp",EDGE,"E2.top");Q0=makeQuery(id+"F12.boolean.opBoolean","MERGE",FACE,{"derivedFrom":[makeQuery(id+"F8.boolean.opBoolean","MERGE",FACE,{"derivedFrom":[makeQuery(id+"F4.boolean.opBoolean","MERGE",FACE,{"derivedFrom":[makeQuery(id+"F2.boolean.opBoolean","MERGE",FACE,{"derivedFrom":[makeQuery(id+"F1.opExtrude","CAP_FACE",FACE,{"disambiguationData":[OSD([sQuery(id+"F0.wireOp",EDGE,"E2.bottom"),subQ0,sQuery(id+"F0.wireOp",EDGE,"E2.left"),sQuery(id+"F0.wireOp",EDGE,"E2.right"),sQuery(id+"F0.wireOp",EDGE,"E3.bottom"),sQuery(id+"F0.wireOp",EDGE,"E3.top"),sQuery(id+"F0.wireOp",EDGE,"E3.left"),sQuery(id+"F0.wireOp",EDGE,"E3.right"),sQuery(id+"F0.wireOp",EDGE,"E4.0.1.0"),sQuery(id+"F0.wireOp",EDGE,"E4.0.1.1"),sQuery(id+"F0.wireOp",EDGE,"E4.0.1.2"),sQuery(id+"F0.wireOp",EDGE,"E4.0.1.3"),sQuery(id+"F0.wireOp",EDGE,"E4.0.2.0"),sQuery(id+"F0.wireOp",EDGE,"E4.0.2.1"),sQuery(id+"F0.wireOp",EDGE,"E4.0.2.2"),sQuery(id+"F0.wireOp",EDGE,"E4.0.2.3"),sQuery(id+"F0.wireOp",EDGE,"E4.0.3.0"),sQuery(id+"F0.wireOp",EDGE,"E4.0.3.1"),sQuery(id+"F0.wireOp",EDGE,"E4.0.3.2"),sQuery(id+"F0.wireOp",EDGE,"E4.0.3.3"),sQuery(id+"F0.wireOp",EDGE,"E4.1.0.0"),sQuery(id+"F0.wireOp",EDGE,"E4.1.0.1"),sQuery(id+"F0.wireOp",EDGE,"E4.1.0.2"),sQuery(id+"F0.wireOp",EDGE,"E4.1.0.3"),sQuery(id+"F0.wireOp",EDGE,"E4.1.1.0"),sQuery(id+"F0.wireOp",EDGE,"E4.1.1.1"),sQuery(id+"F0.wireOp",EDGE,"E4.1.1.2"),sQuery(id+"F0.wireOp",EDGE,"E4.1.1.3"),sQuery(id+"F0.wireOp",EDGE,"E4.1.2.0"),sQuery(id+"F0.wireOp",EDGE,"E4.1.2.1"),sQuery(id+"F0.wireOp",EDGE,"E4.1.2.2"),sQuery(id+"F0.wireOp",EDGE,"E4.1.2.3"),sQuery(id+"F0.wireOp",EDGE,"E4.1.3.0"),sQuery(id+"F0.wireOp",EDGE,"E4.1.3.1"),sQuery(id+"F0.wireOp",EDGE,"E4.1.3.2"),sQuery(id+"F0.wireOp",EDGE,"E4.1.3.3"),sQuery(id+"F0.wireOp",EDGE,"E4.2.0.0"),sQuery(id+"F0.wireOp",EDGE,"E4.2.0.1"),sQuery(id+"F0.wireOp",EDGE,"E4.2.0.2"),sQuery(id+"F0.wireOp",EDGE,"E4.2.0.3"),sQuery(id+"F0.wireOp",EDGE,"E4.2.1.0"),sQuery(id+"F0.wireOp",EDGE,"E4.2.1.1"),sQuery(id+"F0.wireOp",EDGE,"E4.2.1.2"),sQuery(id+"F0.wireOp",EDGE,"E4.2.1.3"),sQuery(id+"F0.wireOp",EDGE,"E4.2.2.0"),sQuery(id+"F0.wireOp",EDGE,"E4.2.2.1"),sQuery(id+"F0.wireOp",EDGE,"E4.2.2.2"),sQuery(id+"F0.wireOp",EDGE,"E4.2.2.3"),sQuery(id+"F0.wireOp",EDGE,"E4.2.3.0"),sQuery(id+"F0.wireOp",EDGE,"E4.2.3.1"),sQuery(id+"F0.wireOp",EDGE,"E4.2.3.2"),sQuery(id+"F0.wireOp",EDGE,"E4.2.3.3"),sQuery(id+"F0.wireOp",EDGE,"E4.3.0.0"),sQuery(id+"F0.wireOp",EDGE,"E4.3.0.1"),sQuery(id+"F0.wireOp",EDGE,"E4.3.0.2"),sQuery(id+"F0.wireOp",EDGE,"E4.3.0.3"),sQuery(id+"F0.wireOp",EDGE,"E4.3.1.0"),sQuery(id+"F0.wireOp",EDGE,"E4.3.1.1"),sQuery(id+"F0.wireOp",EDGE,"E4.3.1.2"),sQuery(id+"F0.wireOp",EDGE,"E4.3.1.3"),sQuery(id+"F0.wireOp",EDGE,"E4.3.2.0"),sQuery(id+"F0.wireOp",EDGE,"E4.3.2.1"),sQuery(id+"F0.wireOp",EDGE,"E4.3.2.2"),sQuery(id+"F0.wireOp",EDGE,"E4.3.2.3"),sQuery(id+"F0.wireOp",EDGE,"E4.3.3.0"),sQuery(id+"F0.wireOp",EDGE,"E4.3.3.1"),sQuery(id+"F0.wireOp",EDGE,"E4.3.3.2"),sQuery(id+"F0.wireOp",EDGE,"E4.3.3.3"),sQuery(id+"F0.wireOp",EDGE,"E4.4.0.0"),sQuery(id+"F0.wireOp",EDGE,"E4.4.0.1"),sQuery(id+"F0.wireOp",EDGE,"E4.4.0.2"),sQuery(id+"F0.wireOp",EDGE,"E4.4.0.3"),sQuery(id+"F0.wireOp",EDGE,"E4.4.1.0"),sQuery(id+"F0.wireOp",EDGE,"E4.4.1.1"),sQuery(id+"F0.wireOp",EDGE,"E4.4.1.2"),sQuery(id+"F0.wireOp",EDGE,"E4.4.1.3"),sQuery(id+"F0.wireOp",EDGE,"E4.4.2.0"),sQuery(id+"F0.wireOp",EDGE,"E4.4.2.1"),sQuery(id+"F0.wireOp",EDGE,"E4.4.2.2"),sQuery(id+"F0.wireOp",EDGE,"E4.4.2.3"),sQuery(id+"F0.wireOp",EDGE,"E4.4.3.0"),sQuery(id+"F0.wireOp",EDGE,"E4.4.3.1"),sQuery(id+"F0.wireOp",EDGE,"E4.4.3.2"),sQuery(id+"F0.wireOp",EDGE,"E4.4.3.3")])],"isStart":false}),makeQuery(id+"F2.opExtrude","SWEPT_FACE",FACE,{"disambiguationData":[OSD([subQ0]),TDD([makeQuery(id+"F1.opExtrude","CAP_EDGE",EDGE,{"disambiguationData":[OSD([subQ0])],"isStart":false})])]})]}),makeQuery(id+"F4.opExtrude","SWEPT_FACE",FACE,{"disambiguationData":[OSD([sQuery(id+"F3.wireOp",EDGE,"E5.bottom")])]})]}),makeQuery(id+"F8.opExtrude","SWEPT_FACE",FACE,{"disambiguationData":[OSD([sQuery(id+"F7.wireOp",EDGE,"E10.bottom")])]})]}),makeQuery(id+"F12.opExtrude","SWEPT_FACE",FACE,{"disambiguationData":[OSD([sQuery(id+"F11.wireOp",EDGE,"E15.bottom")])]})]});}
            var sketch = newSketch(context, id + "F17", { "sketchPlane" : qUnion([Q0])});
            skText(sketch, "E26", { "text": "WP0164X", "fontName": "OpenSans-Bold.ttf"});
            const initialGuessF17  = {"E26": [-0.01701, -0.133, 1, 0, 0.005]};
            skSetInitialGuess(sketch, initialGuessF17);
            skSolve(sketch);
        }
        {
            var Q0;
            Q0 = qSketchRegion(id + "F17", true);
            extrude(context, id + "F18", {"entities" : qUnion([Q0]), "operationType" : NewBodyOperationType.REMOVE, "oppositeDirection" : true, "depth" : 3 * mm});
        }
    });
